# Revit family: JOMA_423
name_source: partatom
category: Structural Connections
revit_build: Autodesk Revit Structure 2012 (Build: 20110309_2315(x64)
units: mm (PartAtom-declared; Revit-internal decimal feet)

## types (4) — shared parameters
Länk Joma Dimensioneringsverktyg = http://www.joma.se
Material = Varmförzinkad stålplåt
t = 2.5 mm  [stored 0.0082021 ft]
zero-valued in all types: Default Elevation

## per-type parameters (varying)
| type | Typ | Vikt | Vinkelbeslag 4230101 | Vinkelbeslag 4230201 | Vinkelbeslag 4230202 | Vinkelbeslag 4230203 | b | h | l |
| 4230201 | VINKEL 4230201 | 0,35 | No | Yes | No | No | 80 mm | 155 mm | 100 mm  [stored 0.328084 ft] |
| 4230101 | VINKEL 4230101 | 0,21 | Yes | No | No | No | 70 mm | 125 mm | 50 mm |
| 4230202 | VINKEL 4230202 | 0,45 | No | No | Yes | No | 80 mm | 155 mm | 160 mm |
| 4230203 | VINKEL 4230203 | 0,30 | No | No | No | Yes | 75 mm | 175 mm | 60 mm |

note: [stored X ft] marks values corroborated as IEEE doubles in the binary element streams (Revit-internal decimal feet)

## geometry (parser evidence)
native form markers: Sweep x3
no freeform markers — native parametric forms only
